# Revit family: IS_Solea_R0110_BIM_DE
name_source: partatom
category: Plumbing Fixtures
revit_build: Autodesk Revit 2017 (Build: 20160225_1515(x64)
units: mm (PartAtom-declared; Revit-internal decimal feet)

## family parameters
Cut with Voids When Loaded = No
Host = Face
OmniClass Number = 23.45.05.21.11.11
OmniClass Title = Water Operated Water Closets
Part Type = Normal
Room Calculation Point = No
Round Connector Dimension = Use Diameter
Shared = Yes

## types (4) — shared parameters
AfstandsEenheid = millimeters
Artikelreferentie = 1
Assembly Code = C1030200
Auteur = Ideal Standrad
BREEAMApproved = No
Beschrijvinggarantie = Manufacturers Warranty
Default Elevation = 900 mm
Douchebak = No
DuurEenheid = year
ECA = No
Garantieunits = Year
Heefthandvaten = No
Hulp = https://www.idealstandard.de
Installatieinstructies = https://www.idealstandard.de
Materiaal = Metal
Merk = Ideal Standard
Montageinstuctie = https://www.idealstandard.de
NBSDescription = WC cistern fittings
NBSReference = 45-30-70/387
Productinformatie = https://www.idealstandard.de
Telefoonnummer = +49 (0) 6571 16 0
URL = https://www.idealstandard.de
Uniclass2 = Pr_40_20_93_89
Uniclass2015Description = Urinal and WC fittings
Uniclass2015Referentie = Pr_40_20_93
Urlproducent = https://www.idealstandard.de
Versie = 1
Verwachtelevensduur = 5
Volumeunits = Litres
WRAS = No
WaterEfficientProduct = No
zero-valued in all types: Breedte, BrutoGewicht, CWFU, Cost, Diepte, GrootteAfvoergat, HWFU, Lengte, Overloop, Vervangingskosten, WFU

## per-type parameters (varying)
| type | Afmetingen | Afwerking | Artikelnummer | Artikelomschrijving | Barcode | BimObjectNaam | Description | Flush Plate Material | Kleur | Model | Nettogewicht |
| R0110AC - SOLEA P2 WHITE - IS | 231 x 146 x 14 mm | White | R0110AC | Betätigungsplatte M1 OLEAS, mechanischen Auslösung, Chrom | 3391500579798 | IS_Ideal Standard_WC cistern fittings_Solea_R0110AC | "Karisma " plate DF (Pneumatic)(White) | Plactic-White | White | R0110AC | 0.368 |
| R0110AA - SOLEA P2 CHROME - IS | 230 x 157 x 7 mm | Chrome | R0115AA | Betätigungsplatte P2 SOLEA, pneumatischen Auslösung, Chrom matt | 3391500580138 | IS_Ideal Standard_WC cistern fittings_Oleas_R0115AA | New 1 Round button plate - mechanical IS | Chrome-Polished | Chrome | R0115AA | 0.3354 |
| R0110JG - SOLEA P2 MATT CHROME - IS | 231 x 146 x 14 mm | Matt Chrome | R0110JG | Betätigungsplatte P2 SOLEA, pneumatischen Auslösung, Schwarz | 3391500580114 | IS_Ideal Standard_WC cistern fittings_Solea_R0110JG | "Karisma " plate DF (Pneumatic) -  Matta Chrome | Chrome-Matt | Matt Chrome | R0110JG | 0.368 |
| R0110A6 - SOLEA P2 BLACK - IS | 231 x 146 x 14 mm | White | R0110A6 | Sensor-Betätigungsplatte NT1 SYMFO, Weiß | 3391500580107 | IS_Ideal Standard_WC cistern fittings_Solea_R0110A6 | Karisma  plate DF (Pneumatic) | Plastic-Black | White | R0110A6 | 0.368 |

## geometry (parser evidence)
native form markers: Sweep x2
no freeform markers — native parametric forms only
